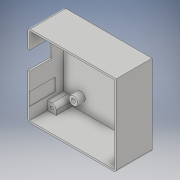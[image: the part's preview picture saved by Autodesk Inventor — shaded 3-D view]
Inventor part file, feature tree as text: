
AUTODESK INVENTOR PART (.ipt)
format: ipt  version: 2019 (Build 230136000, 136)  size: 443,904 bytes
history: native  units: mm
features: other x11, extrude x6, hole x2, loft x1, fillet x1
ambient origin geometry x8: Origin, YZ Plane, XZ Plane, XY Plane, X Axis, Y Axis, Z Axis, Center Point
bodies: Solid1 (feature_tree)
feature tree (21):
  extrude  "Extrusion1"  Depth=78.5mm
  other  "Uchyt_arduino"
  other  "Spojeni_srouby"
  extrude  "Extrusion2"  Depth=72.0mm
  extrude  "Extrusion5"  Depth=1.2mm TaperAngle=0.0deg
  hole  "Hole6"  [1 undecoded]
  extrude  "Extrusion6"  Depth=8.0mm
  extrude  "Extrusion7"  Depth=7.0mm TaperAngle=0.0deg
  hole  "Hole7"  [1 undecoded]
  other  "napajeni_znacka1"
  other  "napajeni_znacka2_rovina"
  loft  "Loft4"
  extrude  "Extrusion8"  Depth=15.45mm
  fillet  "Fillet1"  Radius=1.6mm
  other  "Zakladna"
  other  "diry_srouby"
  other  "steny"
  other  "stena_RJ45"
  other  "arduino_uchyt_zavitovaVlozka"
  other  "napajeni_znacka2"
  other  "vyrez_nepouzity_jack"
note: 2 required parameter values undecoded (feature->parameter linkage not recoverable at this tier; creation-order binding heuristic only, values carry confidence <= 0.55)
